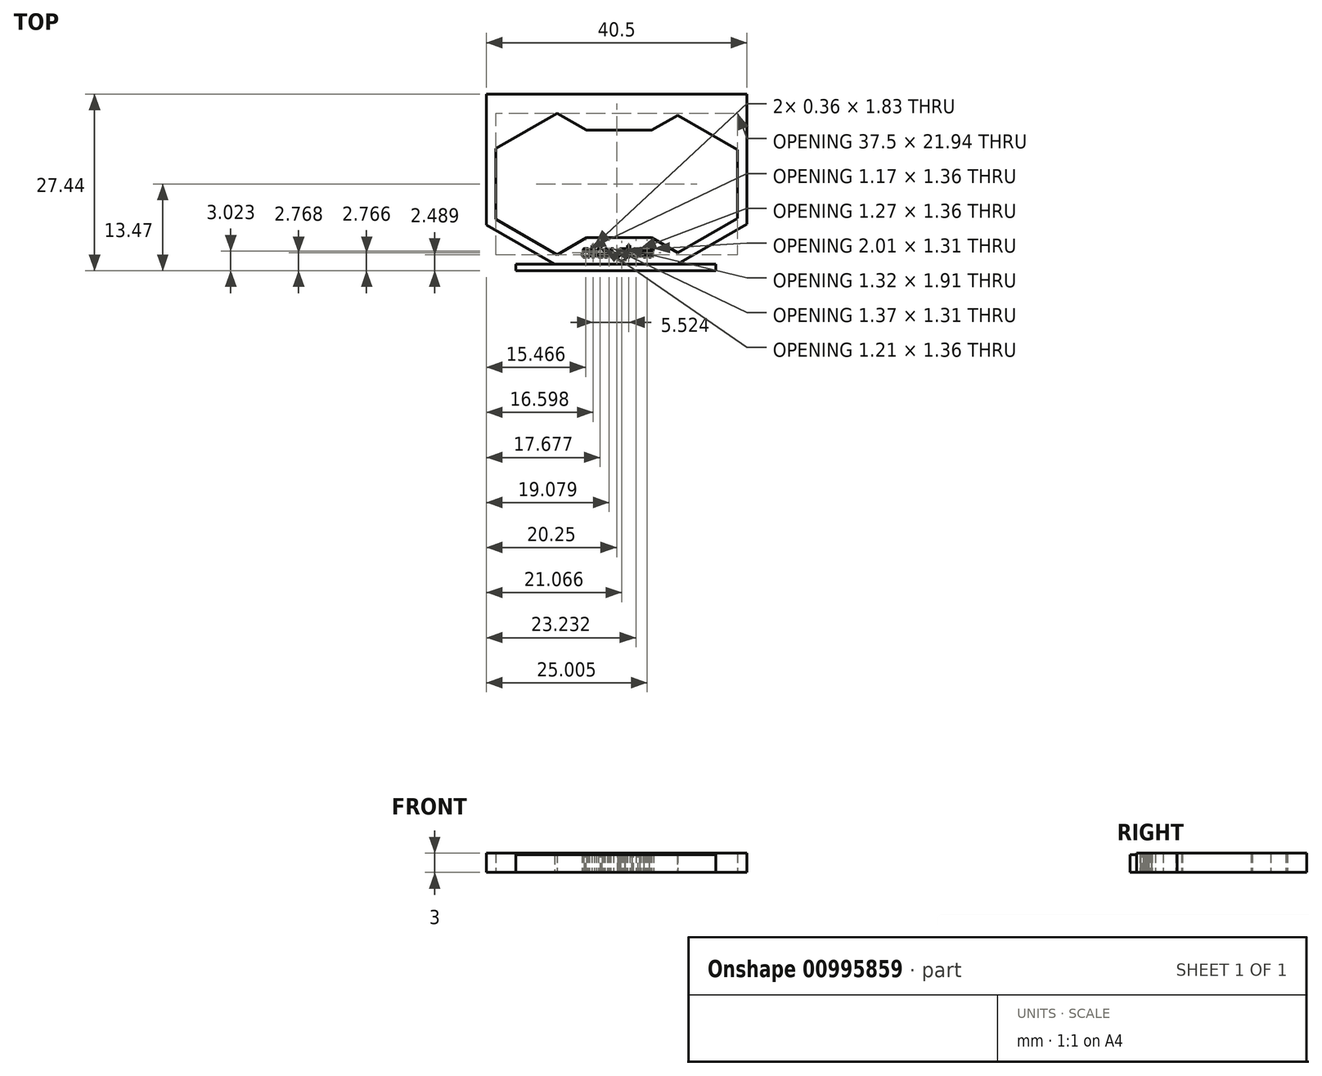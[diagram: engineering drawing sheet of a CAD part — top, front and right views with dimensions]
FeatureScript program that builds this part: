
annotation { "Feature Type Name" : "Feature", "Feature Type Description" : "" }
export const myFeature = defineFeature(function(context is Context, id is Id, definition is map)
    precondition{}
    {
        {
            var Q0;
            Q0=qCreatedBy(makeId("Top.planeOp"),FACE);
            var sketch = newSketch(context, id + "F0", { "sketchPlane" : qUnion([Q0])});
            skCircle(sketch, "E0.cCircle", {"center": v(-9.5, 0) * mm, "radius": 9.5 * mm, "construction": true});
            skLineSegment(sketch, "E0.0", {"start": v(0, 5.48) * mm, "end": v(0, -5.48) * mm});
            skLineSegment(sketch, "E0.1", {"start": v(0, -5.48) * mm, "end": v(-9.5, -10.97) * mm});
            skLineSegment(sketch, "E0.2", {"start": v(-9.5, -10.97) * mm, "end": v(-19, -5.48) * mm});
            skLineSegment(sketch, "E0.3", {"start": v(-19, -5.48) * mm, "end": v(-19, 5.48) * mm});
            skLineSegment(sketch, "E0.4", {"start": v(-19, 5.48) * mm, "end": v(-9.5, 10.97) * mm});
            skLineSegment(sketch, "E0.5", {"start": v(-9.5, 10.97) * mm, "end": v(0, 5.48) * mm});
            skPoint(sketch, "E0.0.midPoint", {"position": v(0, 0) * mm});
            skCircle(sketch, "E1.cCircle", {"center": v(9.25, 0) * mm, "radius": 9.25 * mm, "construction": true});
            skLineSegment(sketch, "E1.0", {"start": v(18.5, 5.34) * mm, "end": v(18.5, -5.34) * mm});
            skLineSegment(sketch, "E1.1", {"start": v(18.5, -5.34) * mm, "end": v(9.25, -10.68) * mm});
            skLineSegment(sketch, "E1.2", {"start": v(9.25, -10.68) * mm, "end": v(0, -5.34) * mm});
            skLineSegment(sketch, "E1.3", {"start": v(0, -5.34) * mm, "end": v(0, 5.34) * mm});
            skLineSegment(sketch, "E1.4", {"start": v(0, 5.34) * mm, "end": v(9.25, 10.68) * mm});
            skLineSegment(sketch, "E1.5", {"start": v(9.25, 10.68) * mm, "end": v(18.5, 5.34) * mm});
            skPoint(sketch, "E1.0.midPoint", {"position": v(18.5, 0) * mm});
            skLineSegment(sketch, "E2.bottom", {"start": v(-20.5, 13.97) * mm, "end": v(20, 13.97) * mm});
            skLineSegment(sketch, "E2.top", {"start": v(-20.5, -12.47) * mm, "end": v(20, -12.47) * mm});
            skLineSegment(sketch, "E2.left", {"start": v(-20.5, 13.97) * mm, "end": v(-20.5, -12.47) * mm});
            skLineSegment(sketch, "E2.right", {"start": v(20, 13.97) * mm, "end": v(20, -12.47) * mm});
            skLineSegment(sketch, "E3", {"start": v(-20.5, -6.35) * mm, "end": v(-9.9, -12.47) * mm});
            skLineSegment(sketch, "E4", {"start": v(20, -6.2) * mm, "end": v(9.15, -12.47) * mm});
            skPoint(sketch, "E5", {"position": v(0, 8.34) * mm});
            skPoint(sketch, "E6", {"position": v(0, -8.34) * mm});
            skLineSegment(sketch, "E7", {"start": v(-4.95, 8.34) * mm, "end": v(5.2, 8.34) * mm});
            skLineSegment(sketch, "E8", {"start": v(-4.95, -8.34) * mm, "end": v(5.2, -8.34) * mm});
            skText(sketch, "E9", { "text": "alex glow", "fontName": "OpenSans-Bold.ttf"});
            const initialGuessF0  = {"E9": [-0.00572, -0.01136, 1, 0, 0.00173]};
            skSetInitialGuess(sketch, initialGuessF0);
            skSolve(sketch);
        }
        {
            var Q0;
            {var subQ10=sQuery(id+"F0.wireOp",EDGE,"E0.2");Q0=makeQuery(id+"F0.imprint","IMPRINT",FACE,{"disambiguationData":[TD([[makeQuery(id+"F0.imprint","IMPRINT",EDGE,{"derivedFrom":subQ10}),1.0]])]});}
            extrude(context, id + "F1", {"entities" : qUnion([Q0]), "flatOperationType" : FlatOperationType.REMOVE, "depth" : 3 * mm, "offsetDistance" : 25 * mm, "domain" : OperationDomain.MODEL});
        }
        {
            var Q0;
            Q0=makeQuery(id+"F1.opExtrude","SWEPT_FACE",FACE,{"disambiguationData":[OSD([sQuery(id+"F0.wireOp",EDGE,"E2.top")])]});
            var sketch = newSketch(context, id + "F2", { "sketchPlane" : qUnion([Q0])});
            skLineSegment(sketch, "E10.bottom", {"start": v(-15.9, 3) * mm, "end": v(15.15, 3) * mm});
            skLineSegment(sketch, "E10.top", {"start": v(-15.9, 0) * mm, "end": v(15.15, 0) * mm});
            skLineSegment(sketch, "E10.left", {"start": v(-15.9, 3) * mm, "end": v(-15.9, 0) * mm});
            skLineSegment(sketch, "E10.right", {"start": v(15.15, 3) * mm, "end": v(15.15, 0) * mm});
            skLineSegment(sketch, "E11.bottom", {"start": v(-15.9, 2.75) * mm, "end": v(15.15, 2.75) * mm});
            skLineSegment(sketch, "E11.left", {"start": v(-15.9, 2.75) * mm, "end": v(-15.9, 0) * mm});
            skLineSegment(sketch, "E11.right", {"start": v(15.15, 2.75) * mm, "end": v(15.15, 0) * mm});
            skSolve(sketch);
        }
        {
            var Q0;
            {var subQ0=sQuery(id+"F2.wireOp",EDGE,"E10.top");var subQ3=sQuery(id+"F2.wireOp",EDGE,"E10.left");var subQ4=makeQuery(id+"F2.imprint","INTERSECT",VERTEX,{"derivedFrom":[subQ0,subQ3]});Q0=makeQuery(id+"F2.imprint","IMPRINT",FACE,{"disambiguationData":[TD([[makeQuery(id+"F2.imprint","IMPRINT",EDGE,{"disambiguationData":[TD([[subQ4,1.0]])],"derivedFrom":subQ3}),1.0]])]});}
            var Q1;
            {var subQ0=sQuery(id+"F2.wireOp",EDGE,"E10.top");var subQ1=sQuery(id+"F0.wireOp",EDGE,"E2.top");var subQ2=makeQuery(id+"F1.opExtrude","SWEPT_EDGE",EDGE,{"disambiguationData":[OSD([subQ1,sQuery(id+"F0.wireOp",EDGE,"E3")])]});var subQ3=makeQuery(id+"F2.imprint","INTERSECT",VERTEX,{"derivedFrom":[subQ2,subQ0]});Q1=makeQuery(id+"F2.imprint","IMPRINT",FACE,{"disambiguationData":[TD([[makeQuery(id+"F2.imprint","IMPRINT",EDGE,{"disambiguationData":[TD([[subQ3,-1.0]])],"derivedFrom":subQ0}),1.0]])]});}
            var Q2;
            {var subQ0=sQuery(id+"F2.wireOp",EDGE,"E10.top");var subQ3=sQuery(id+"F2.wireOp",EDGE,"E10.right");var subQ4=makeQuery(id+"F2.imprint","INTERSECT",VERTEX,{"derivedFrom":[subQ0,subQ3]});Q2=makeQuery(id+"F2.imprint","IMPRINT",FACE,{"disambiguationData":[TD([[makeQuery(id+"F2.imprint","IMPRINT",EDGE,{"disambiguationData":[TD([[subQ4,1.0]])],"derivedFrom":subQ3}),-1.0]])]});}
            extrude(context, id + "F3", {"entities" : qUnion([Q0, Q1, Q2]), "operationType" : NewBodyOperationType.ADD, "depth" : 1 * mm, "offsetDistance" : 25 * mm});
        }
    });
